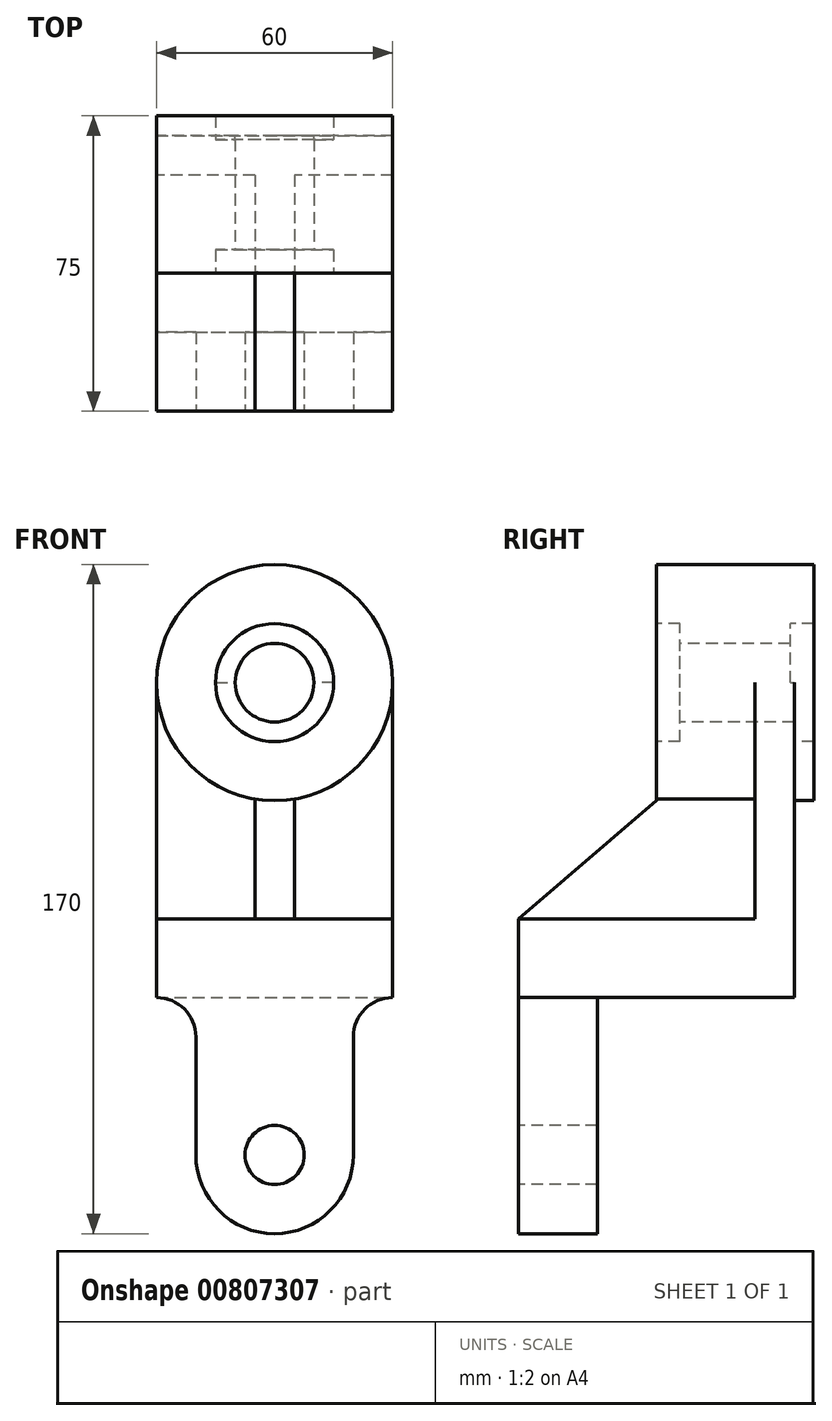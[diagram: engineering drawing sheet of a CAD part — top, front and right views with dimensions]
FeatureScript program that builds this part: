
annotation { "Feature Type Name" : "Feature", "Feature Type Description" : "" }
export const myFeature = defineFeature(function(context is Context, id is Id, definition is map)
    precondition{}
    {
        {
            var Q0;
            Q0=qCreatedBy(makeId("Front.planeOp"),FACE);
            var sketch = newSketch(context, id + "F0", { "sketchPlane" : qUnion([Q0])});
            skCircle(sketch, "E0", {"center": v(0, 0) * mm, "radius": 7.5 * mm});
            skLineSegment(sketch, "E1", {"start": v(-20, 0) * mm, "end": v(-20, 30) * mm});
            skLineSegment(sketch, "E2", {"start": v(0, 0) * mm, "end": v(0, 60) * mm, "construction": true});
            skLineSegment(sketch, "E3", {"start": v(-30, 60) * mm, "end": v(30, 60) * mm});
            skPoint(sketch, "E4", {"position": v(0, 60) * mm});
            skLineSegment(sketch, "E5", {"start": v(-30, 60) * mm, "end": v(-30, 40) * mm});
            skLineSegment(sketch, "E6", {"start": v(-30, 40) * mm, "end": v(-30, 40) * mm});
            skPoint(sketch, "E7.visualSharp", {"position": v(-20, 40) * mm});
            skArc(sketch, "E7.filletArc", {"start": v(-20, 30) * mm, "mid": v(-22.93, 37.07) * mm, "end": v(-30, 40) * mm});
            skLineSegment(sketch, "E8.MirrorCS", {"start": v(30, 60) * mm, "end": v(30, 40) * mm});
            skArc(sketch, "E9.MirrorCS", {"start": v(20, 30) * mm, "mid": v(22.93, 37.07) * mm, "end": v(30, 40) * mm});
            skLineSegment(sketch, "E10.MirrorCS", {"start": v(20, 0) * mm, "end": v(20, 30) * mm});
            skArc(sketch, "E11", {"start": v(-20, 0) * mm, "mid": v(0, -20) * mm, "end": v(20, 0) * mm});
            skLineSegment(sketch, "E12", {"start": v(-30, 40) * mm, "end": v(30, 40) * mm});
            skSolve(sketch);
        }
        {
            var Q0;
            Q0=qSketchRegion(id+"F0",true);
            extrude(context, id + "F1", {"entities" : qUnion([Q0]), "oppositeDirection" : true, "depth" : 20 * mm, "offsetDistance" : 25 * mm});
        }
        {
            var Q0;
            Q0=makeQuery(id+"F0.imprint","IMPRINT",FACE,{"disambiguationData":[TD([[makeQuery(id+"F0.imprint","IMPRINT",EDGE,{"derivedFrom":sQuery(id+"F0.wireOp",EDGE,"E3")}),-1.0]])]});
            extrude(context, id + "F2", {"entities" : qUnion([Q0]), "operationType" : NewBodyOperationType.ADD, "oppositeDirection" : true, "depth" : 70 * mm, "offsetDistance" : 25 * mm});
        }
        {
            var Q0;
            Q0=qCreatedBy(makeId("Right.planeOp"),FACE);
            var sketch = newSketch(context, id + "F3", { "sketchPlane" : qUnion([Q0])});
            skLineSegment(sketch, "E13.0.0", {"start": v(0, 60) * mm, "end": v(0, 40) * mm});
            skLineSegment(sketch, "E13.0.1", {"start": v(0, 40) * mm, "end": v(20, 40) * mm});
            skLineSegment(sketch, "E13.0.2", {"start": v(20, 40) * mm, "end": v(70, 40) * mm});
            skLineSegment(sketch, "E13.0.3", {"start": v(70, 40) * mm, "end": v(70, 60) * mm});
            skLineSegment(sketch, "E13.0.4", {"start": v(70, 60) * mm, "end": v(0, 60) * mm});
            skLineSegment(sketch, "E14", {"start": v(75, 60) * mm, "end": v(75, 150) * mm});
            skLineSegment(sketch, "E15.bottom", {"start": v(75, 150) * mm, "end": v(35, 150) * mm});
            skLineSegment(sketch, "E15.top", {"start": v(75, 90) * mm, "end": v(35, 90) * mm});
            skLineSegment(sketch, "E15.left", {"start": v(75, 150) * mm, "end": v(75, 90) * mm});
            skLineSegment(sketch, "E15.right", {"start": v(35, 150) * mm, "end": v(35, 90) * mm});
            skPoint(sketch, "E16", {"position": v(35, 120) * mm});
            skLineSegment(sketch, "E17", {"start": v(35, 120) * mm, "end": v(75, 120) * mm});
            skLineSegment(sketch, "E18", {"start": v(41, 150) * mm, "end": v(41, 90) * mm});
            skLineSegment(sketch, "E19", {"start": v(35, 135) * mm, "end": v(75, 135) * mm});
            skLineSegment(sketch, "E20", {"start": v(41, 130) * mm, "end": v(75, 130) * mm});
            skLineSegment(sketch, "E21.MirrorCS", {"start": v(35, 105) * mm, "end": v(75, 105) * mm});
            skLineSegment(sketch, "E22.MirrorCS", {"start": v(41, 110) * mm, "end": v(75, 110) * mm});
            skLineSegment(sketch, "E23", {"start": v(60, 120) * mm, "end": v(60, 60) * mm});
            skLineSegment(sketch, "E24", {"start": v(70, 120) * mm, "end": v(70, 60) * mm});
            skLineSegment(sketch, "E25", {"start": v(35, 90) * mm, "end": v(0, 60) * mm});
            skLineSegment(sketch, "E26", {"start": v(35, 90) * mm, "end": v(52.5, 105) * mm});
            skLineSegment(sketch, "E27", {"start": v(69, 150) * mm, "end": v(69, 90) * mm});
            skLineSegment(sketch, "E28", {"start": v(70, 60) * mm, "end": v(75, 60) * mm});
            skSolve(sketch);
        }
        {
            var Q0;
            {var subQ0=sQuery(id+"F3.wireOp",EDGE,"E20");var subQ1=sQuery(id+"F3.wireOp",EDGE,"E18");var subQ2=makeQuery(id+"F3.imprint","INTERSECT",VERTEX,{"derivedFrom":[subQ1,subQ0]});Q0=makeQuery(id+"F3.imprint","IMPRINT",FACE,{"disambiguationData":[TD([[makeQuery(id+"F3.imprint","IMPRINT",EDGE,{"disambiguationData":[TD([[subQ2,1.0]])],"derivedFrom":subQ1}),1.0]])]});}
            var Q1;
            {var subQ0=sQuery(id+"F3.wireOp",EDGE,"E15.right");var subQ1=sQuery(id+"F3.wireOp",EDGE,"E15.bottom");var subQ2=makeQuery(id+"F3.imprint","INTERSECT",VERTEX,{"derivedFrom":[subQ1,subQ0]});Q1=makeQuery(id+"F3.imprint","IMPRINT",FACE,{"disambiguationData":[TD([[makeQuery(id+"F3.imprint","IMPRINT",EDGE,{"disambiguationData":[TD([[subQ2,1.0]])],"derivedFrom":subQ1}),1.0]])]});}
            var Q2;
            {var subQ0=sQuery(id+"F3.wireOp",EDGE,"E15.left");var subQ1=sQuery(id+"F3.wireOp",EDGE,"E15.bottom");var subQ2=makeQuery(id+"F3.imprint","INTERSECT",VERTEX,{"derivedFrom":[subQ1,subQ0]});Q2=makeQuery(id+"F3.imprint","IMPRINT",FACE,{"disambiguationData":[TD([[makeQuery(id+"F3.imprint","IMPRINT",EDGE,{"disambiguationData":[TD([[subQ2,-1.0]])],"derivedFrom":subQ1}),1.0]])]});}
            var Q3;
            {var subQ0=sQuery(id+"F3.wireOp",EDGE,"E18");var subQ1=sQuery(id+"F3.wireOp",EDGE,"E15.bottom");var subQ2=makeQuery(id+"F3.imprint","INTERSECT",VERTEX,{"derivedFrom":[subQ1,subQ0]});Q3=makeQuery(id+"F3.imprint","IMPRINT",FACE,{"disambiguationData":[TD([[makeQuery(id+"F3.imprint","IMPRINT",EDGE,{"disambiguationData":[TD([[subQ2,1.0]])],"derivedFrom":subQ1}),1.0]])]});}
            var Q4;
            Q4=sQuery(id+"F3.wireOp",EDGE,"E17");
            revolve(context, id + "F4", {"surfaceOperationType" : NewSurfaceOperationType.NEW, "entities" : qUnion([Q0, Q1, Q2, Q3]), "axis" : qUnion([Q4]), "revolveType" : RevolveType.FULL});
        }
        {
            var Q0;
            {var subQ0=sQuery(id+"F3.wireOp",EDGE,"E23");var subQ1=sQuery(id+"F3.wireOp",EDGE,"E13.0.4");var subQ2=makeQuery(id+"F3.imprint","INTERSECT",VERTEX,{"derivedFrom":[subQ1,subQ0]});Q0=makeQuery(id+"F3.imprint","IMPRINT",FACE,{"disambiguationData":[TD([[makeQuery(id+"F3.imprint","IMPRINT",EDGE,{"disambiguationData":[TD([[subQ2,1.0]])],"derivedFrom":subQ1}),-1.0]])]});}
            var Q1;
            {var subQ0=sQuery(id+"F3.wireOp",EDGE,"E24");var subQ1=sQuery(id+"F3.wireOp",EDGE,"E15.top");var subQ2=makeQuery(id+"F3.imprint","INTERSECT",VERTEX,{"derivedFrom":[subQ1,subQ0]});Q1=makeQuery(id+"F3.imprint","IMPRINT",FACE,{"disambiguationData":[TD([[makeQuery(id+"F3.imprint","IMPRINT",EDGE,{"disambiguationData":[TD([[subQ2,-1.0]])],"derivedFrom":subQ1}),-1.0]])]});}
            var Q2;
            {var subQ0=sQuery(id+"F3.wireOp",EDGE,"E23");var subQ1=sQuery(id+"F3.wireOp",EDGE,"E21.MirrorCS");var subQ2=makeQuery(id+"F3.imprint","INTERSECT",VERTEX,{"derivedFrom":[subQ1,subQ0]});Q2=makeQuery(id+"F3.imprint","IMPRINT",FACE,{"disambiguationData":[TD([[makeQuery(id+"F3.imprint","IMPRINT",EDGE,{"disambiguationData":[TD([[subQ2,-1.0]])],"derivedFrom":subQ1}),1.0]])]});}
            var Q3;
            {var subQ0=sQuery(id+"F3.wireOp",EDGE,"E23");var subQ1=sQuery(id+"F3.wireOp",EDGE,"E17");var subQ2=makeQuery(id+"F3.imprint","INTERSECT",VERTEX,{"derivedFrom":[subQ1,subQ0]});Q3=makeQuery(id+"F3.imprint","IMPRINT",FACE,{"disambiguationData":[TD([[makeQuery(id+"F3.imprint","IMPRINT",EDGE,{"disambiguationData":[TD([[subQ2,-1.0]])],"derivedFrom":subQ1}),-1.0]])]});}
            var Q4;
            {var subQ0=sQuery(id+"F3.wireOp",EDGE,"E27");var subQ1=sQuery(id+"F3.wireOp",EDGE,"E15.top");var subQ2=makeQuery(id+"F3.imprint","INTERSECT",VERTEX,{"derivedFrom":[subQ1,subQ0]});Q4=makeQuery(id+"F3.imprint","IMPRINT",FACE,{"disambiguationData":[TD([[makeQuery(id+"F3.imprint","IMPRINT",EDGE,{"disambiguationData":[TD([[subQ2,-1.0]])],"derivedFrom":subQ1}),-1.0]])]});}
            var Q5;
            {var subQ0=sQuery(id+"F3.wireOp",EDGE,"E24");var subQ1=sQuery(id+"F3.wireOp",EDGE,"E17");var subQ2=makeQuery(id+"F3.imprint","INTERSECT",VERTEX,{"derivedFrom":[subQ1,subQ0]});Q5=makeQuery(id+"F3.imprint","IMPRINT",FACE,{"disambiguationData":[TD([[makeQuery(id+"F3.imprint","IMPRINT",EDGE,{"disambiguationData":[TD([[subQ2,1.0]])],"derivedFrom":subQ1}),-1.0]])]});}
            var Q6;
            {var subQ0=sQuery(id+"F3.wireOp",EDGE,"E27");var subQ1=sQuery(id+"F3.wireOp",EDGE,"E21.MirrorCS");var subQ2=makeQuery(id+"F3.imprint","INTERSECT",VERTEX,{"derivedFrom":[subQ1,subQ0]});Q6=makeQuery(id+"F3.imprint","IMPRINT",FACE,{"disambiguationData":[TD([[makeQuery(id+"F3.imprint","IMPRINT",EDGE,{"disambiguationData":[TD([[subQ2,-1.0]])],"derivedFrom":subQ1}),1.0]])]});}
            extrude(context, id + "F5", {"entities" : qUnion([Q0, Q1, Q2, Q3, Q4, Q5, Q6]), "operationType" : NewBodyOperationType.ADD, "endBound" : BoundingType.SYMMETRIC, "depth" : 60 * mm, "offsetDistance" : 25 * mm});
        }
        {
            var Q0;
            {var subQ5=sQuery(id+"F3.wireOp",EDGE,"E25");Q0=makeQuery(id+"F3.imprint","IMPRINT",FACE,{"disambiguationData":[TD([[makeQuery(id+"F3.imprint","IMPRINT",EDGE,{"derivedFrom":subQ5}),1.0]])]});}
            var Q1;
            {var subQ1=sQuery(id+"F3.wireOp",EDGE,"E15.top");var subQ3=sQuery(id+"F3.wireOp",EDGE,"E18");var subQ4=makeQuery(id+"F3.imprint","INTERSECT",VERTEX,{"derivedFrom":[subQ1,subQ3]});Q1=makeQuery(id+"F3.imprint","IMPRINT",FACE,{"disambiguationData":[TD([[makeQuery(id+"F3.imprint","IMPRINT",EDGE,{"disambiguationData":[TD([[subQ4,1.0]])],"derivedFrom":subQ3}),-1.0]])]});}
            var Q2;
            {var subQ1=sQuery(id+"F3.wireOp",EDGE,"E15.top");var subQ7=sQuery(id+"F3.wireOp",EDGE,"E18");var subQ8=makeQuery(id+"F3.imprint","INTERSECT",VERTEX,{"derivedFrom":[subQ1,subQ7]});Q2=makeQuery(id+"F3.imprint","IMPRINT",FACE,{"disambiguationData":[TD([[makeQuery(id+"F3.imprint","IMPRINT",EDGE,{"disambiguationData":[TD([[subQ8,1.0]])],"derivedFrom":subQ1}),-1.0]])]});}
            extrude(context, id + "F6", {"entities" : qUnion([Q0, Q1, Q2]), "operationType" : NewBodyOperationType.ADD, "endBound" : BoundingType.SYMMETRIC, "depth" : 10 * mm, "offsetDistance" : 25 * mm});
        }
        {
            var Q0;
            {var subQ2=sQuery(id+"F3.wireOp",EDGE,"E17");var subQ6=sQuery(id+"F3.wireOp",EDGE,"E15.right");var subQ7=makeQuery(id+"F3.imprint","INTERSECT",VERTEX,{"derivedFrom":[subQ6,subQ2]});Q0=makeQuery(id+"F3.imprint","IMPRINT",FACE,{"disambiguationData":[TD([[makeQuery(id+"F3.imprint","IMPRINT",EDGE,{"disambiguationData":[TD([[subQ7,1.0]])],"derivedFrom":subQ6}),1.0]])]});}
            var Q1;
            {var subQ4=sQuery(id+"F3.wireOp",EDGE,"E20");Q1=makeQuery(id+"F3.imprint","IMPRINT",FACE,{"disambiguationData":[TD([[makeQuery(id+"F3.imprint","IMPRINT",EDGE,{"derivedFrom":subQ4}),-1.0]])]});}
            var Q2;
            {var subQ0=sQuery(id+"F3.wireOp",EDGE,"E19");var subQ1=sQuery(id+"F3.wireOp",EDGE,"E15.left");var subQ2=makeQuery(id+"F3.imprint","INTERSECT",VERTEX,{"derivedFrom":[subQ1,subQ0]});Q2=makeQuery(id+"F3.imprint","IMPRINT",FACE,{"disambiguationData":[TD([[makeQuery(id+"F3.imprint","IMPRINT",EDGE,{"disambiguationData":[TD([[subQ2,-1.0]])],"derivedFrom":subQ1}),-1.0]])]});}
            var Q3;
            Q3=sQuery(id+"F3.wireOp",EDGE,"E17");
            revolve(context, id + "F7", {"operationType" : NewBodyOperationType.REMOVE, "surfaceOperationType" : NewSurfaceOperationType.NEW, "entities" : qUnion([Q0, Q1, Q2]), "axis" : qUnion([Q3]), "revolveType" : RevolveType.FULL, "oppositeDirection" : true});
        }
    });
